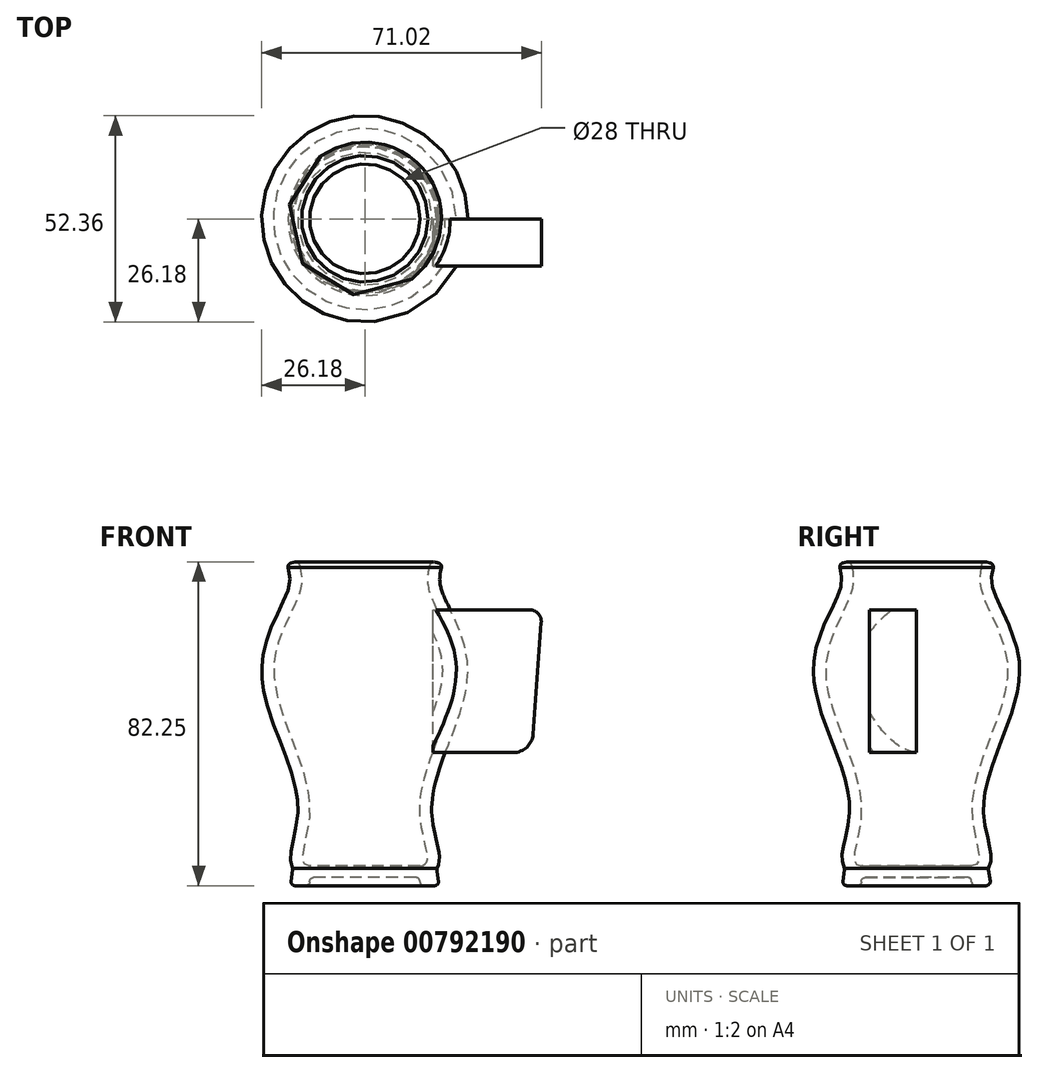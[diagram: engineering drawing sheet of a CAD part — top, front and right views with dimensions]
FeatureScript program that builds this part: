
annotation { "Feature Type Name" : "Feature", "Feature Type Description" : "" }
export const myFeature = defineFeature(function(context is Context, id is Id, definition is map)
    precondition{}
    {
        {
            var Q0;
            Q0=qCreatedBy(makeId("Front.planeOp"),FACE);
            var sketch = newSketch(context, id + "F0", { "sketchPlane" : qUnion([Q0])});
            skLineSegment(sketch, "E0", {"start": v(0, -34.97) * mm, "end": v(14, -34.97) * mm});
            skFitSpline(sketch, "E1", {"points": [v(14, -34.97) * mm, v(14, -21.5) * mm, v(23.16, 14.43) * mm, v(16.49, 34.7) * mm, v(16.75, 42.4) * mm], "startDerivative": vector(58.18, 0) * mm, "endDerivative": vector(9.82, 44.13) * mm});
            skFitSpline(sketch, "E2.0", {"points": [v(14, -37.97) * mm, v(14.26, -37.97) * mm, v(14.8, -37.94) * mm, v(15.64, -37.77) * mm, v(16.5, -37.43) * mm, v(17.32, -36.88) * mm, v(17.98, -36.16) * mm, v(18.44, -35.37) * mm, v(18.72, -34.6) * mm, v(18.9, -33.62) * mm, v(18.92, -32.54) * mm, v(18.8, -31.32) * mm, v(18.57, -30.11) * mm, v(18.3, -28.88) * mm, v(18, -27.61) * mm, v(17.7, -26.3) * mm, v(17.43, -24.98) * mm, v(17.2, -23.64) * mm, v(17.07, -22.52) * mm, v(17, -21.64) * mm, v(16.98, -20.76) * mm, v(17, -19.64) * mm, v(17.12, -18.25) * mm, v(17.32, -16.82) * mm, v(17.7, -14.86) * mm, v(18.36, -12.34) * mm, v(19.37, -9.22) * mm, v(20.92, -4.97) * mm, v(22.62, -0.62) * mm, v(24.15, 3.76) * mm, v(25.13, 7.06) * mm, v(25.73, 9.82) * mm, v(26.04, 12.04) * mm, v(26.16, 13.71) * mm, v(26.17, 15.39) * mm, v(26.05, 17.01) * mm, v(25.83, 18.6) * mm, v(25.42, 20.63) * mm, v(24.72, 23.05) * mm, v(23.7, 25.74) * mm, v(22.59, 28.23) * mm, v(21.5, 30.5) * mm, v(20.68, 32.21) * mm, v(20.13, 33.45) * mm, v(19.78, 34.3) * mm, v(19.55, 34.95) * mm, v(19.4, 35.42) * mm, v(19.28, 35.85) * mm, v(19.17, 36.37) * mm, v(19.07, 37.15) * mm, v(19.04, 38.07) * mm, v(19.15, 39.2) * mm, v(19.37, 40.4) * mm, v(19.57, 41.28) * mm, v(19.67, 41.74) * mm]});
            skLineSegment(sketch, "E2.1", {"start": v(0, -37.97) * mm, "end": v(13, -37.97) * mm});
            skLineSegment(sketch, "E3", {"start": v(14, -38.97) * mm, "end": v(14, -39.05) * mm});
            skLineSegment(sketch, "E4", {"start": v(15, -40.05) * mm, "end": v(17.72, -40.05) * mm});
            skLineSegment(sketch, "E5", {"start": v(18.7, -38.9) * mm, "end": v(18.3, -36) * mm});
            skPoint(sketch, "E6.visualSharp", {"position": v(18.25, -35.68) * mm});
            skArc(sketch, "E6.filletArc", {"start": v(18.39, -35.42) * mm, "mid": v(18.3, -35.7) * mm, "end": v(18.3, -36) * mm});
            skPoint(sketch, "E7.visualSharp", {"position": v(18.87, -40.05) * mm});
            skArc(sketch, "E7.filletArc", {"start": v(17.72, -40.05) * mm, "mid": v(18.47, -39.7) * mm, "end": v(18.7, -38.9) * mm});
            skPoint(sketch, "E8.visualSharp", {"position": v(14, -37.97) * mm});
            skArc(sketch, "E8.filletArc", {"start": v(14, -38.97) * mm, "mid": v(13.7, -38.26) * mm, "end": v(13, -37.97) * mm});
            skPoint(sketch, "E9.visualSharp", {"position": v(14, -40.05) * mm});
            skArc(sketch, "E9.filletArc", {"start": v(14, -39.05) * mm, "mid": v(14.3, -39.75) * mm, "end": v(15, -40.05) * mm});
            skLineSegment(sketch, "E10", {"start": v(17.72, 42.18) * mm, "end": v(18.7, 41.96) * mm});
            skArc(sketch, "E11.filletArc", {"start": v(17.72, 42.18) * mm, "mid": v(16.97, 42.04) * mm, "end": v(16.53, 41.41) * mm});
            skPoint(sketch, "E12.visualSharp", {"position": v(19.67, 41.74) * mm});
            skArc(sketch, "E12.filletArc", {"start": v(19.46, 40.77) * mm, "mid": v(19.32, 41.52) * mm, "end": v(18.7, 41.96) * mm});
            skLineSegment(sketch, "E13", {"start": v(0, -34.97) * mm, "end": v(0, -37.97) * mm});
            skPoint(sketch, "E14.end.orphan", {"position": v(7.44, 34.31) * mm});
            skPoint(sketch, "E15.trimOffspring.end.orphan", {"position": v(7.44, -9.27) * mm});
            skSolve(sketch);
        }
        {
            var Q0;
            Q0=makeQuery(id+"F0.imprint","IMPRINT",FACE,{"disambiguationData":[TD([[makeQuery(id+"F0.imprint","IMPRINT",EDGE,{"derivedFrom":sQuery(id+"F0.wireOp",EDGE,"E0")}),-1.0]])]});
            var Q1;
            {var subQ0=sQuery(id+"F0.wireOp",EDGE,"9zlEg6yF-YewB-EKoW-vldd-4ht7yD9abJlT");Q1=makeQuery(id+"F0.imprint","IMPRINT",FACE,{"disambiguationData":[TD([[makeQuery(id+"F0.imprint","IMPRINT",EDGE,{"derivedFrom":subQ0}),-1.0]])]});}
            var Q2;
            Q2=makeQuery(id+"F0.imprint","IMPRINT",FACE,{"disambiguationData":[TD([[makeQuery(id+"F0.imprint","IMPRINT",EDGE,{"derivedFrom":sQuery(id+"F0.wireOp",EDGE,"E10")}),-1.0]])]});
            var Q3;
            Q3=sQuery(id+"F0.wireOp",EDGE,"E13");
            revolve(context, id + "F1", {"surfaceOperationType" : NewSurfaceOperationType.NEW, "entities" : qUnion([Q0, Q1, Q2]), "axis" : qUnion([Q3]), "revolveType" : RevolveType.FULL});
        }
        {
            var Q0;
            Q0=qCreatedBy(makeId("Front.planeOp"),FACE);
            var sketch = newSketch(context, id + "F2", { "sketchPlane" : qUnion([Q0])});
            skLineSegment(sketch, "E16", {"start": v(17.33, 30.07) * mm, "end": v(41.84, 30.07) * mm});
            skLineSegment(sketch, "E17", {"start": v(44.83, 26.85) * mm, "end": v(42.75, -1.6) * mm});
            skLineSegment(sketch, "E18", {"start": v(37.76, -6.23) * mm, "end": v(17.33, -6.23) * mm});
            skLineSegment(sketch, "E19", {"start": v(17.33, -6.23) * mm, "end": v(17.33, 30.07) * mm});
            skPoint(sketch, "E20.visualSharp", {"position": v(45.06, 30.07) * mm});
            skArc(sketch, "E20.filletArc", {"start": v(44.83, 26.85) * mm, "mid": v(44.03, 29.11) * mm, "end": v(41.84, 30.07) * mm});
            skPoint(sketch, "E21.visualSharp", {"position": v(42.41, -6.23) * mm});
            skArc(sketch, "E21.filletArc", {"start": v(37.76, -6.23) * mm, "mid": v(41.17, -4.9) * mm, "end": v(42.75, -1.6) * mm});
            skSolve(sketch);
        }
        {
            var Q0;
            Q0 = qSketchRegion(id + "F2", true);
            extrude(context, id + "F3", {"entities" : qUnion([Q0]), "operationType" : NewBodyOperationType.ADD, "depth" : 12 * mm, "offsetDistance" : 25 * mm});
        }
    });
